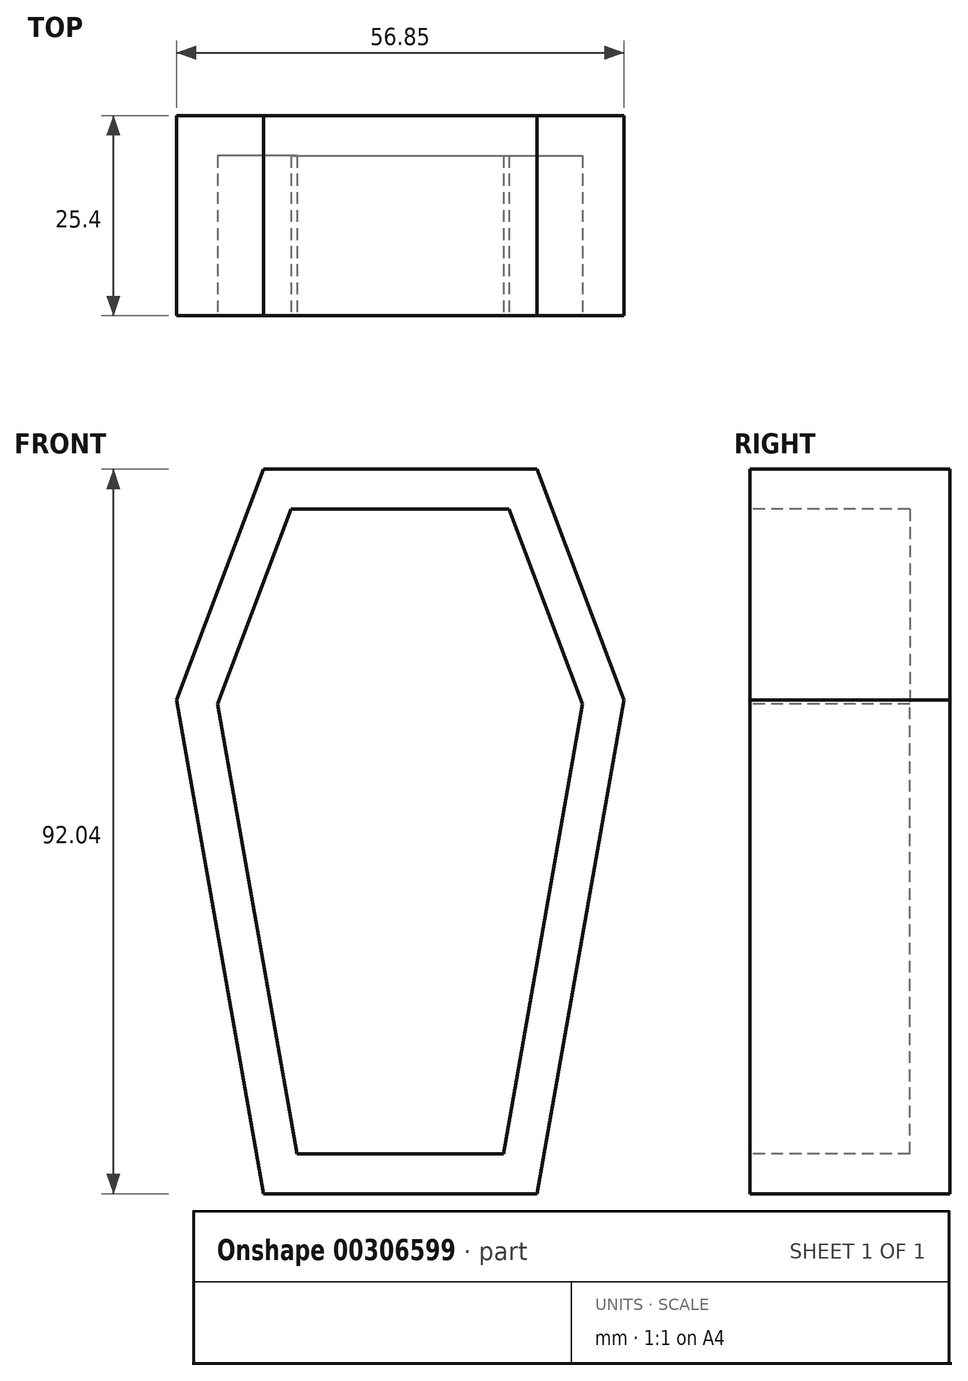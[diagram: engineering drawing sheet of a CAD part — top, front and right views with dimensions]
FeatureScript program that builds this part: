
annotation { "Feature Type Name" : "Feature", "Feature Type Description" : "" }
export const myFeature = defineFeature(function(context is Context, id is Id, definition is map)
    precondition{}
    {
        {
            var Q0;
            Q0=qCreatedBy(makeId("Front.planeOp"),FACE);
            var sketch = newSketch(context, id + "F0", { "sketchPlane" : qUnion([Q0])});
            skLineSegment(sketch, "E0", {"start": v(-11.82, -52.29) * mm, "end": v(22.92, -52.29) * mm});
            skLineSegment(sketch, "E1", {"start": v(-11.82, -52.29) * mm, "end": v(-22.87, 10.4) * mm});
            skLineSegment(sketch, "E2", {"start": v(22.92, -52.29) * mm, "end": v(33.98, 10.4) * mm});
            skLineSegment(sketch, "E3", {"start": v(-11.82, 39.75) * mm, "end": v(22.92, 39.75) * mm});
            skLineSegment(sketch, "E4", {"start": v(-11.82, 39.75) * mm, "end": v(-22.87, 10.4) * mm});
            skLineSegment(sketch, "E5", {"start": v(22.92, 39.75) * mm, "end": v(33.98, 10.4) * mm});
            skSolve(sketch);
        }
        {
            var Q0;
            Q0 = qSketchRegion(id + "F0", true);
            extrude(context, id + "F1", {"entities" : qUnion([Q0]), "oppositeDirection" : true, "depth" : 25.4 * mm});
        }
        {
            var Q0;
            Q0=makeQuery(id+"F1.opExtrude","CAP_FACE",FACE,{"disambiguationData":[OSD([sQuery(id+"F0.wireOp",EDGE,"E0"),sQuery(id+"F0.wireOp",EDGE,"E1"),sQuery(id+"F0.wireOp",EDGE,"E2"),sQuery(id+"F0.wireOp",EDGE,"E3"),sQuery(id+"F0.wireOp",EDGE,"E4"),sQuery(id+"F0.wireOp",EDGE,"E5")])],"isStart":true});
            shell(context, id + "F2", {"entities" : qUnion([Q0]), "thickness" : 5.08 * mm});
        }
    });
